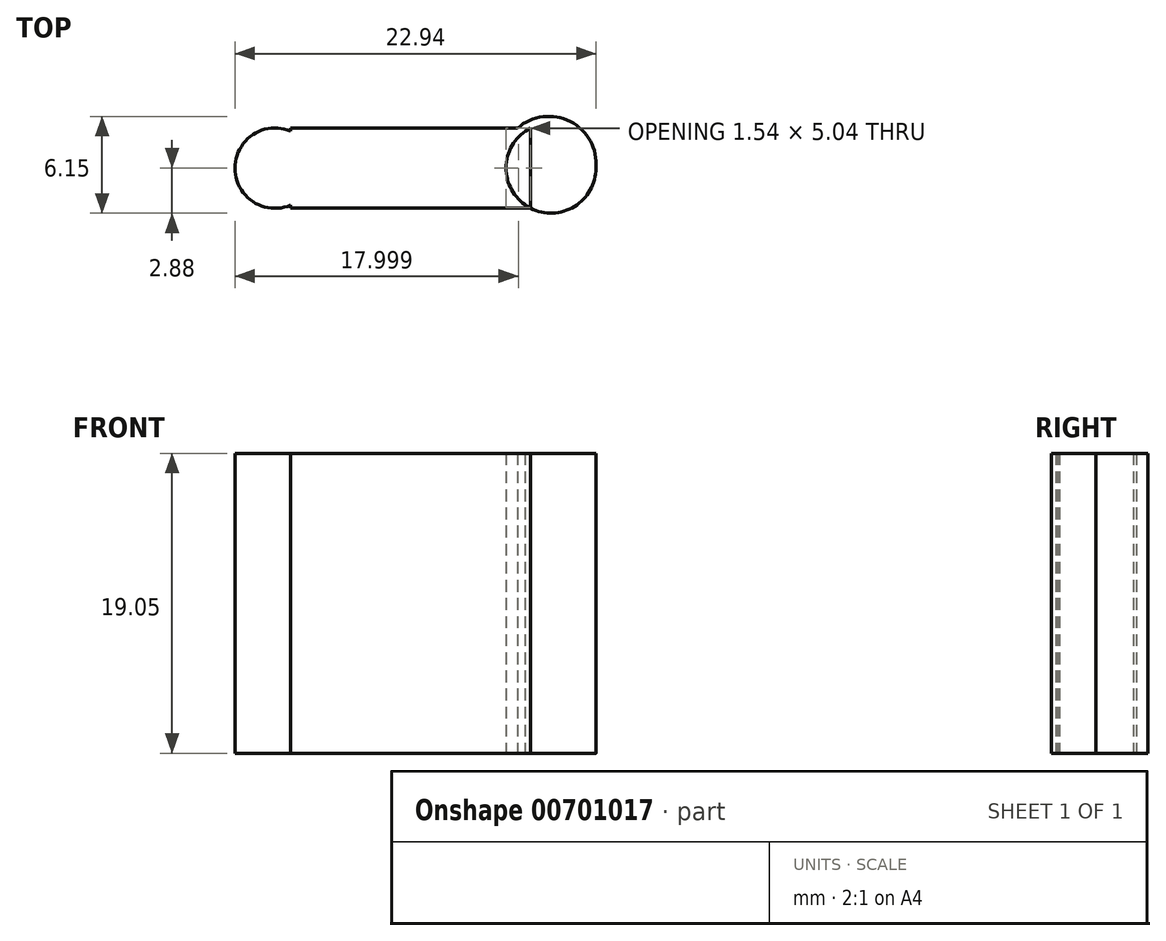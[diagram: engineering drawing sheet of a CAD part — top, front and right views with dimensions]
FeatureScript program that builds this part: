
annotation { "Feature Type Name" : "Feature", "Feature Type Description" : "" }
export const myFeature = defineFeature(function(context is Context, id is Id, definition is map)
    precondition{}
    {
        {
            var Q0;
            Q0=qCreatedBy(makeId("Top.planeOp"),FACE);
            var sketch = newSketch(context, id + "F0", { "sketchPlane" : qUnion([Q0])});
            skLineSegment(sketch, "E0.bottom", {"start": v(7.62, -2.54) * mm, "end": v(-7.62, -2.54) * mm});
            skLineSegment(sketch, "E0.top", {"start": v(7.62, 2.54) * mm, "end": v(-7.62, 2.54) * mm});
            skLineSegment(sketch, "E0.left", {"start": v(7.62, -2.54) * mm, "end": v(7.62, 2.54) * mm});
            skLineSegment(sketch, "E0.right", {"start": v(-7.62, -2.54) * mm, "end": v(-7.62, 2.54) * mm});
            skPoint(sketch, "E0.middle", {"position": v(0, 0) * mm});
            skArc(sketch, "E1", {"start": v(7.62, 2.54) * mm, "mid": v(7.44, -2.44) * mm, "end": v(11.78, 0) * mm});
            skArc(sketch, "E2", {"start": v(-11.32, 0) * mm, "mid": v(-7.05, -2.24) * mm, "end": v(-7.62, 2.54) * mm});
            skLineSegment(sketch, "E3", {"start": v(-7.62, 2.54) * mm, "end": v(-7.62, 2.54) * mm});
            skLineSegment(sketch, "E4", {"start": v(7.62, 2.54) * mm, "end": v(7.62, 2.54) * mm});
            skCircle(sketch, "E5", {"center": v(-8.6, 0) * mm, "radius": 2.55 * mm});
            skCircle(sketch, "E6", {"center": v(8.78, 0.28) * mm, "radius": 3.01 * mm});
            skSolve(sketch);
        }
        {
            var Q0;
            Q0 = qSketchRegion(id + "F0", true);
            var Q1;
            {var subQ0=sQuery(id+"F0.wireOp",EDGE,"E0.bottom");Q1=makeQuery(id+"F0.imprint","IMPRINT",FACE,{"disambiguationData":[TD([[makeQuery(id+"F0.imprint","IMPRINT",EDGE,{"derivedFrom":subQ0}),-1.0]])]});}
            extrude(context, id + "F1", {"entities" : qUnion([Q0, Q1]), "depth" : 19.05 * mm, "offsetDistance" : 25.4 * mm});
        }
    });
